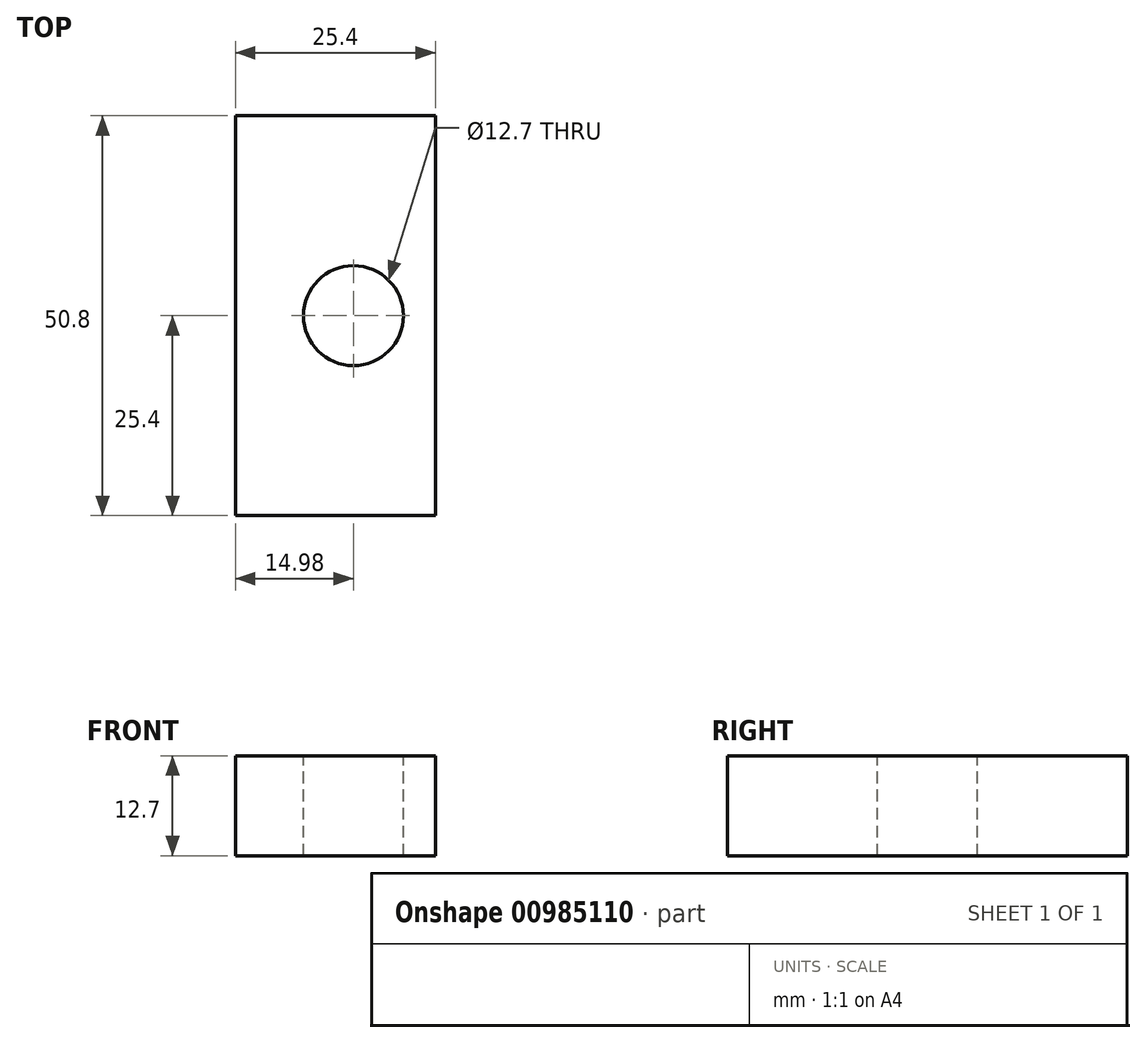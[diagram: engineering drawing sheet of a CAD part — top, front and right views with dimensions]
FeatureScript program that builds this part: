
annotation { "Feature Type Name" : "Feature", "Feature Type Description" : "" }
export const myFeature = defineFeature(function(context is Context, id is Id, definition is map)
    precondition{}
    {
        {
            var Q0;
            Q0=qCreatedBy(makeId("Top.planeOp"),FACE);
            var sketch = newSketch(context, id + "F0", { "sketchPlane" : qUnion([Q0])});
            skLineSegment(sketch, "E0.bottom", {"start": v(-14.98, -25.4) * mm, "end": v(10.42, -25.4) * mm});
            skLineSegment(sketch, "E0.top", {"start": v(-14.98, 25.4) * mm, "end": v(10.42, 25.4) * mm});
            skLineSegment(sketch, "E0.left", {"start": v(-14.98, -25.4) * mm, "end": v(-14.98, 25.4) * mm});
            skLineSegment(sketch, "E0.right", {"start": v(10.42, -25.4) * mm, "end": v(10.42, 25.4) * mm});
            skPoint(sketch, "E0.middle", {"position": v(-2.28, 0) * mm});
            skSolve(sketch);
        }
        {
            var Q0;
            Q0 = qSketchRegion(id + "F0", true);
            var Q1;
            Q1=makeQuery(id+"F0.imprint","IMPRINT",FACE,{"disambiguationData":[TD([[makeQuery(id+"F0.imprint","IMPRINT",EDGE,{"derivedFrom":sQuery(id+"F0.wireOp",EDGE,"E0.bottom")}),1.0]])]});
            extrude(context, id + "F1", {"entities" : qUnion([Q0, Q1]), "depth" : 12.7 * mm, "offsetDistance" : 25.4 * mm});
        }
        {
            var Q0;
            Q0=makeQuery(id+"F1.opExtrude","CAP_FACE",FACE,{"disambiguationData":[OSD([sQuery(id+"F0.wireOp",EDGE,"E0.bottom"),sQuery(id+"F0.wireOp",EDGE,"E0.top"),sQuery(id+"F0.wireOp",EDGE,"E0.left"),sQuery(id+"F0.wireOp",EDGE,"E0.right")])],"isStart":false});
            var sketch = newSketch(context, id + "F2", { "sketchPlane" : qUnion([Q0])});
            skCircle(sketch, "E1", {"center": v(0, 0) * mm, "radius": 6.35 * mm});
            skSolve(sketch);
        }
        {
            var Q0;
            Q0=makeQuery(id+"F2.imprint","IMPRINT",FACE,{"disambiguationData":[TD([[makeQuery(id+"F2.imprint","IMPRINT",EDGE,{"derivedFrom":sQuery(id+"F2.wireOp",EDGE,"E1")}),1.0]])]});
            extrude(context, id + "F3", {"entities" : qUnion([Q0]), "operationType" : NewBodyOperationType.REMOVE, "oppositeDirection" : true, "depth" : 24.38 * mm, "offsetDistance" : 25.4 * mm});
        }
    });
